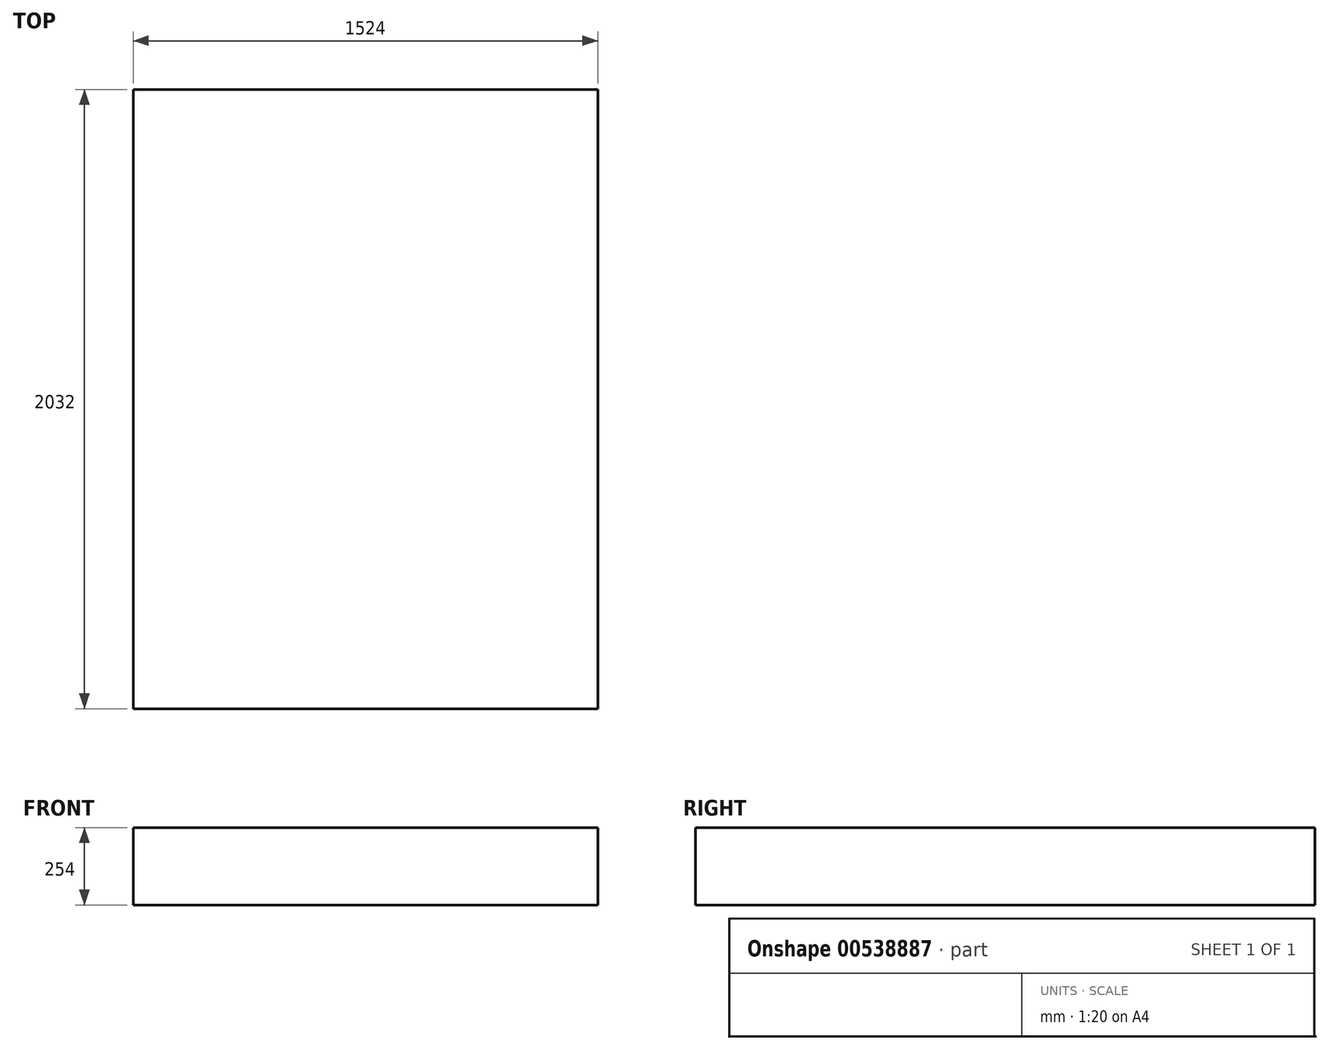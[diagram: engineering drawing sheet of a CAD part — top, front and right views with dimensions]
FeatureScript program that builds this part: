
annotation { "Feature Type Name" : "Feature", "Feature Type Description" : "" }
export const myFeature = defineFeature(function(context is Context, id is Id, definition is map)
    precondition{}
    {
        {
            var Q0;
            Q0=qCreatedBy(makeId("Front.planeOp"),FACE);
            var sketch = newSketch(context, id + "F0", { "sketchPlane" : qUnion([Q0])});
            skLineSegment(sketch, "E0.bottom", {"start": v(-762, 254) * mm, "end": v(762, 254) * mm});
            skLineSegment(sketch, "E0.top", {"start": v(-762, 0) * mm, "end": v(762, 0) * mm});
            skLineSegment(sketch, "E0.left", {"start": v(-762, 254) * mm, "end": v(-762, 0) * mm});
            skLineSegment(sketch, "E0.right", {"start": v(762, 254) * mm, "end": v(762, 0) * mm});
            skSolve(sketch);
        }
        {
            var Q0;
            Q0=makeQuery(id+"F0.imprint","IMPRINT",FACE,{"disambiguationData":[TD([[makeQuery(id+"F0.imprint","IMPRINT",EDGE,{"derivedFrom":sQuery(id+"F0.wireOp",EDGE,"E0.bottom")}),-1.0]])]});
            extrude(context, id + "F1", {"entities" : qUnion([Q0]), "depth" : 2032 * mm, "offsetDistance" : 25.4 * mm});
        }
    });
